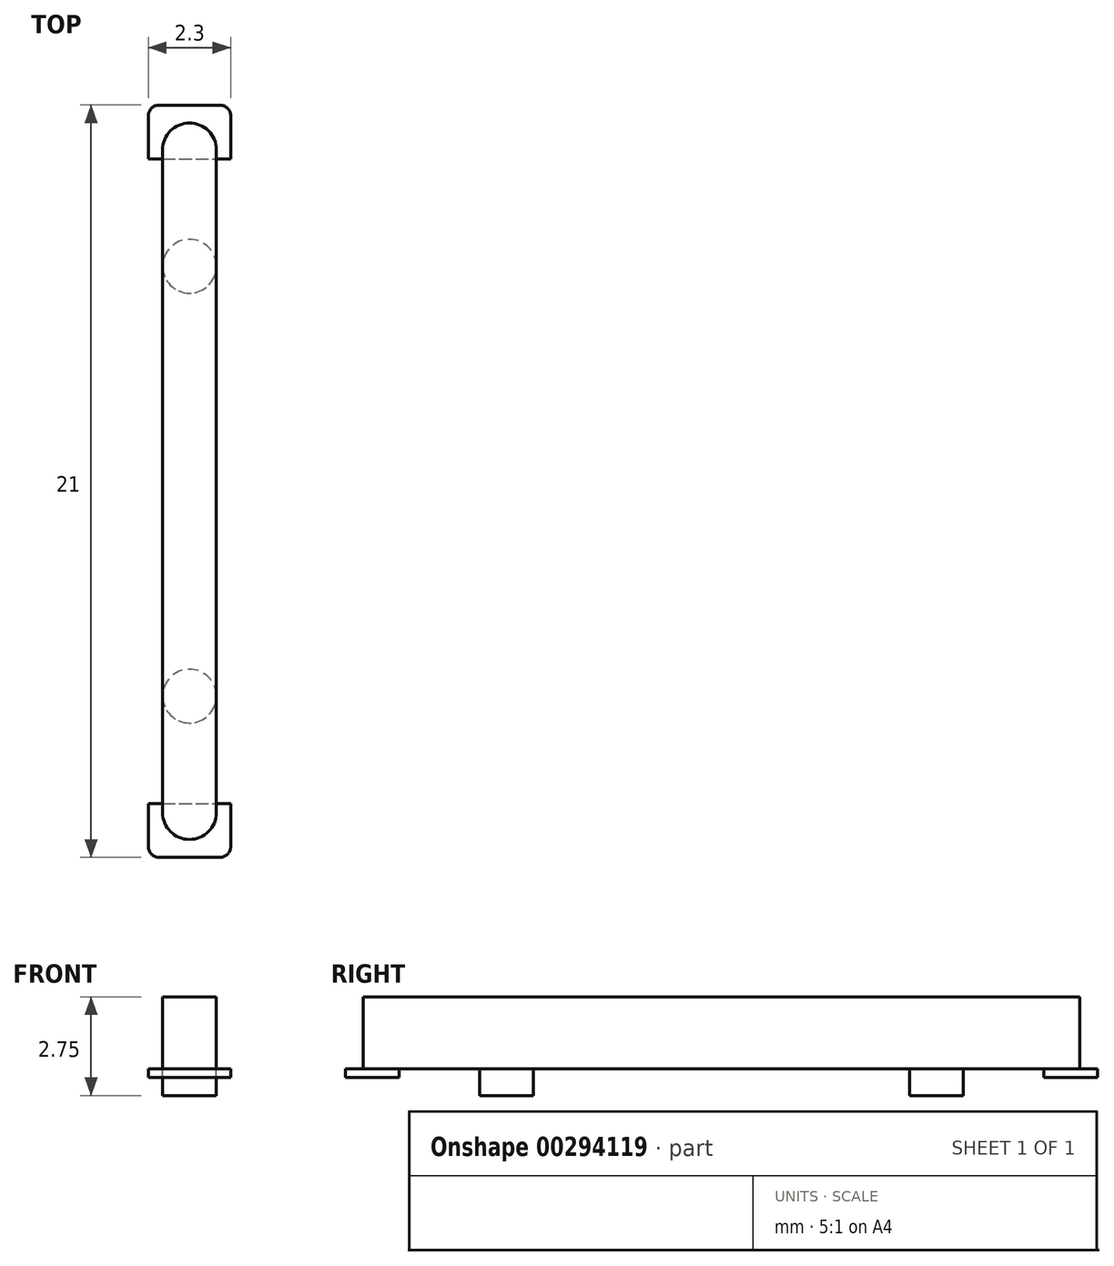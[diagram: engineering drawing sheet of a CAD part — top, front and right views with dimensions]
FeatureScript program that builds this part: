
annotation { "Feature Type Name" : "Feature", "Feature Type Description" : "" }
export const myFeature = defineFeature(function(context is Context, id is Id, definition is map)
    precondition{}
    {
        {
            var Q0;
            Q0=qCreatedBy(makeId("Top.planeOp"),FACE);
            var sketch = newSketch(context, id + "F0", { "sketchPlane" : qUnion([Q0])});
            skLineSegment(sketch, "E0.bottom", {"start": v(-1.5, 9.68) * mm, "end": v(0, 9.68) * mm});
            skLineSegment(sketch, "E0.top", {"start": v(-1.5, -10.32) * mm, "end": v(0, -10.32) * mm});
            skLineSegment(sketch, "E0.left", {"start": v(-1.5, 9.68) * mm, "end": v(-1.5, -10.32) * mm});
            skLineSegment(sketch, "E0.right", {"start": v(0, 9.68) * mm, "end": v(0, -10.32) * mm});
            skPoint(sketch, "E1", {"position": v(-1.5, 5.68) * mm});
            skPoint(sketch, "E2", {"position": v(-1.5, -6.32) * mm});
            skCircle(sketch, "E3", {"center": v(-0.75, 5.68) * mm, "radius": 0.75 * mm});
            skPoint(sketch, "E3.second.point", {"position": v(0, 5.68) * mm});
            skPoint(sketch, "E3.third.point", {"position": v(-0.52, 4.96) * mm});
            skCircle(sketch, "E4", {"center": v(-0.75, -6.32) * mm, "radius": 0.75 * mm});
            skPoint(sketch, "E4.second.point", {"position": v(0, -6.32) * mm});
            skPoint(sketch, "E4.third.point", {"position": v(-0.69, -7.07) * mm});
            skPoint(sketch, "E5", {"position": v(-1.5, 8.68) * mm});
            skPoint(sketch, "E6", {"position": v(-1.5, -9.32) * mm});
            skLineSegment(sketch, "E7.bottom", {"start": v(-1.9, 8.68) * mm, "end": v(0.4, 8.68) * mm});
            skLineSegment(sketch, "E7.top", {"start": v(-1.9, 10.18) * mm, "end": v(0.4, 10.18) * mm});
            skLineSegment(sketch, "E7.left", {"start": v(-1.9, 8.68) * mm, "end": v(-1.9, 10.18) * mm});
            skLineSegment(sketch, "E7.right", {"start": v(0.4, 8.68) * mm, "end": v(0.4, 10.18) * mm});
            skLineSegment(sketch, "E8.bottom", {"start": v(-1.9, -9.32) * mm, "end": v(0.4, -9.32) * mm});
            skLineSegment(sketch, "E8.top", {"start": v(-1.9, -10.82) * mm, "end": v(0.4, -10.82) * mm});
            skLineSegment(sketch, "E8.left", {"start": v(-1.9, -9.32) * mm, "end": v(-1.9, -10.82) * mm});
            skLineSegment(sketch, "E8.right", {"start": v(0.4, -9.32) * mm, "end": v(0.4, -10.82) * mm});
            skSolve(sketch);
        }
        {
            var Q0;
            {var subQ0=sQuery(id+"F0.wireOp",EDGE,"E0.bottom");Q0=makeQuery(id+"F0.imprint","IMPRINT",FACE,{"disambiguationData":[TD([[makeQuery(id+"F0.imprint","IMPRINT",EDGE,{"derivedFrom":subQ0}),-1.0]])]});}
            var Q1;
            {var subQ0=sQuery(id+"F0.wireOp",EDGE,"E7.bottom");var subQ1=sQuery(id+"F0.wireOp",EDGE,"E0.left");var subQ2=makeQuery(id+"F0.imprint","INTERSECT",VERTEX,{"derivedFrom":[subQ1,subQ0]});Q1=makeQuery(id+"F0.imprint","IMPRINT",FACE,{"disambiguationData":[TD([[makeQuery(id+"F0.imprint","IMPRINT",EDGE,{"disambiguationData":[TD([[subQ2,-1.0]])],"derivedFrom":subQ1}),1.0]])]});}
            var Q2;
            {var subQ0=sQuery(id+"F0.wireOp",EDGE,"E3");var subQ1=makeQuery(id+"F0.imprint","INTERSECT",VERTEX,{"derivedFrom":[sQuery(id+"F0.wireOp",EDGE,"E0.left"),subQ0]});Q2=makeQuery(id+"F0.imprint","IMPRINT",FACE,{"disambiguationData":[TD([[makeQuery(id+"F0.imprint","IMPRINT",EDGE,{"disambiguationData":[TD([[subQ1,1.0]])],"derivedFrom":subQ0}),1.0]])]});}
            var Q3;
            {var subQ0=sQuery(id+"F0.wireOp",EDGE,"E3");var subQ1=sQuery(id+"F0.wireOp",EDGE,"E0.left");var subQ2=makeQuery(id+"F0.imprint","INTERSECT",VERTEX,{"derivedFrom":[subQ1,subQ0]});Q3=makeQuery(id+"F0.imprint","IMPRINT",FACE,{"disambiguationData":[TD([[makeQuery(id+"F0.imprint","IMPRINT",EDGE,{"disambiguationData":[TD([[subQ2,-1.0]])],"derivedFrom":subQ1}),1.0]])]});}
            var Q4;
            {var subQ0=sQuery(id+"F0.wireOp",EDGE,"E4");var subQ1=makeQuery(id+"F0.imprint","INTERSECT",VERTEX,{"derivedFrom":[sQuery(id+"F0.wireOp",EDGE,"E0.left"),subQ0]});Q4=makeQuery(id+"F0.imprint","IMPRINT",FACE,{"disambiguationData":[TD([[makeQuery(id+"F0.imprint","IMPRINT",EDGE,{"disambiguationData":[TD([[subQ1,1.0]])],"derivedFrom":subQ0}),1.0]])]});}
            var Q5;
            {var subQ0=sQuery(id+"F0.wireOp",EDGE,"E4");var subQ1=sQuery(id+"F0.wireOp",EDGE,"E0.left");var subQ2=makeQuery(id+"F0.imprint","INTERSECT",VERTEX,{"derivedFrom":[subQ1,subQ0]});Q5=makeQuery(id+"F0.imprint","IMPRINT",FACE,{"disambiguationData":[TD([[makeQuery(id+"F0.imprint","IMPRINT",EDGE,{"disambiguationData":[TD([[subQ2,-1.0]])],"derivedFrom":subQ1}),1.0]])]});}
            var Q6;
            {var subQ0=sQuery(id+"F0.wireOp",EDGE,"E0.top");Q6=makeQuery(id+"F0.imprint","IMPRINT",FACE,{"disambiguationData":[TD([[makeQuery(id+"F0.imprint","IMPRINT",EDGE,{"derivedFrom":subQ0}),1.0]])]});}
            extrude(context, id + "F1", {"entities" : qUnion([Q0, Q1, Q2, Q3, Q4, Q5, Q6]), "depth" : 2 * mm});
        }
        {
            var Q0;
            {var subQ0=sQuery(id+"F0.wireOp",EDGE,"E0.top");Q0=makeQuery(id+"F0.imprint","IMPRINT",FACE,{"disambiguationData":[TD([[makeQuery(id+"F0.imprint","IMPRINT",EDGE,{"derivedFrom":subQ0}),1.0]])]});}
            var Q1;
            {var subQ5=sQuery(id+"F0.wireOp",EDGE,"E0.top");Q1=makeQuery(id+"F0.imprint","IMPRINT",FACE,{"disambiguationData":[TD([[makeQuery(id+"F0.imprint","IMPRINT",EDGE,{"derivedFrom":subQ5}),-1.0]])]});}
            var Q2;
            {var subQ5=sQuery(id+"F0.wireOp",EDGE,"E0.bottom");Q2=makeQuery(id+"F0.imprint","IMPRINT",FACE,{"disambiguationData":[TD([[makeQuery(id+"F0.imprint","IMPRINT",EDGE,{"derivedFrom":subQ5}),1.0]])]});}
            var Q3;
            {var subQ0=sQuery(id+"F0.wireOp",EDGE,"E0.bottom");Q3=makeQuery(id+"F0.imprint","IMPRINT",FACE,{"disambiguationData":[TD([[makeQuery(id+"F0.imprint","IMPRINT",EDGE,{"derivedFrom":subQ0}),-1.0]])]});}
            extrude(context, id + "F2", {"entities" : qUnion([Q0, Q1, Q2, Q3]), "operationType" : NewBodyOperationType.ADD, "oppositeDirection" : true, "depth" : 0.25 * mm});
        }
        {
            var Q0;
            {var subQ0=sQuery(id+"F0.wireOp",EDGE,"E4");var subQ1=makeQuery(id+"F0.imprint","INTERSECT",VERTEX,{"derivedFrom":[sQuery(id+"F0.wireOp",EDGE,"E0.left"),subQ0]});Q0=makeQuery(id+"F0.imprint","IMPRINT",FACE,{"disambiguationData":[TD([[makeQuery(id+"F0.imprint","IMPRINT",EDGE,{"disambiguationData":[TD([[subQ1,1.0]])],"derivedFrom":subQ0}),1.0]])]});}
            var Q1;
            {var subQ0=sQuery(id+"F0.wireOp",EDGE,"E3");var subQ1=makeQuery(id+"F0.imprint","INTERSECT",VERTEX,{"derivedFrom":[sQuery(id+"F0.wireOp",EDGE,"E0.left"),subQ0]});Q1=makeQuery(id+"F0.imprint","IMPRINT",FACE,{"disambiguationData":[TD([[makeQuery(id+"F0.imprint","IMPRINT",EDGE,{"disambiguationData":[TD([[subQ1,1.0]])],"derivedFrom":subQ0}),1.0]])]});}
            extrude(context, id + "F3", {"entities" : qUnion([Q0, Q1]), "operationType" : NewBodyOperationType.ADD, "oppositeDirection" : true, "depth" : 0.75 * mm});
        }
        {
            var Q0;
            Q0=makeQuery(id+"F1.opExtrude","SWEPT_EDGE",EDGE,{"disambiguationData":[OSD([sQuery(id+"F0.wireOp",EDGE,"E0.bottom"),sQuery(id+"F0.wireOp",EDGE,"E0.right")])]});
            var Q1;
            Q1=makeQuery(id+"F1.opExtrude","SWEPT_EDGE",EDGE,{"disambiguationData":[OSD([sQuery(id+"F0.wireOp",EDGE,"E0.bottom"),sQuery(id+"F0.wireOp",EDGE,"E0.left")])]});
            var Q2;
            Q2=makeQuery(id+"F1.opExtrude","SWEPT_EDGE",EDGE,{"disambiguationData":[OSD([sQuery(id+"F0.wireOp",EDGE,"E0.top"),sQuery(id+"F0.wireOp",EDGE,"E0.right")])]});
            var Q3;
            Q3=makeQuery(id+"F1.opExtrude","SWEPT_EDGE",EDGE,{"disambiguationData":[OSD([sQuery(id+"F0.wireOp",EDGE,"E0.top"),sQuery(id+"F0.wireOp",EDGE,"E0.left")])]});
            fillet(context, id + "F4", {"entities" : qUnion([Q0, Q1, Q2, Q3]), "radius" : 0.75 * mm, "tangentPropagation" : true, "allowEdgeOverflow" : false});
        }
        {
            var Q0;
            Q0=makeQuery(id+"F2.opExtrude","SWEPT_EDGE",EDGE,{"disambiguationData":[OSD([sQuery(id+"F0.wireOp",EDGE,"E7.top"),sQuery(id+"F0.wireOp",EDGE,"E7.right")])]});
            var Q1;
            Q1=makeQuery(id+"F2.opExtrude","SWEPT_EDGE",EDGE,{"disambiguationData":[OSD([sQuery(id+"F0.wireOp",EDGE,"E7.top"),sQuery(id+"F0.wireOp",EDGE,"E7.left")])]});
            var Q2;
            Q2=makeQuery(id+"F2.opExtrude","SWEPT_EDGE",EDGE,{"disambiguationData":[OSD([sQuery(id+"F0.wireOp",EDGE,"E8.top"),sQuery(id+"F0.wireOp",EDGE,"E8.right")])]});
            var Q3;
            Q3=makeQuery(id+"F2.opExtrude","SWEPT_EDGE",EDGE,{"disambiguationData":[OSD([sQuery(id+"F0.wireOp",EDGE,"E8.top"),sQuery(id+"F0.wireOp",EDGE,"E8.left")])]});
            fillet(context, id + "F5", {"entities" : qUnion([Q0, Q1, Q2, Q3]), "radius" : 0.3 * mm, "tangentPropagation" : true, "allowEdgeOverflow" : false});
        }
    });
